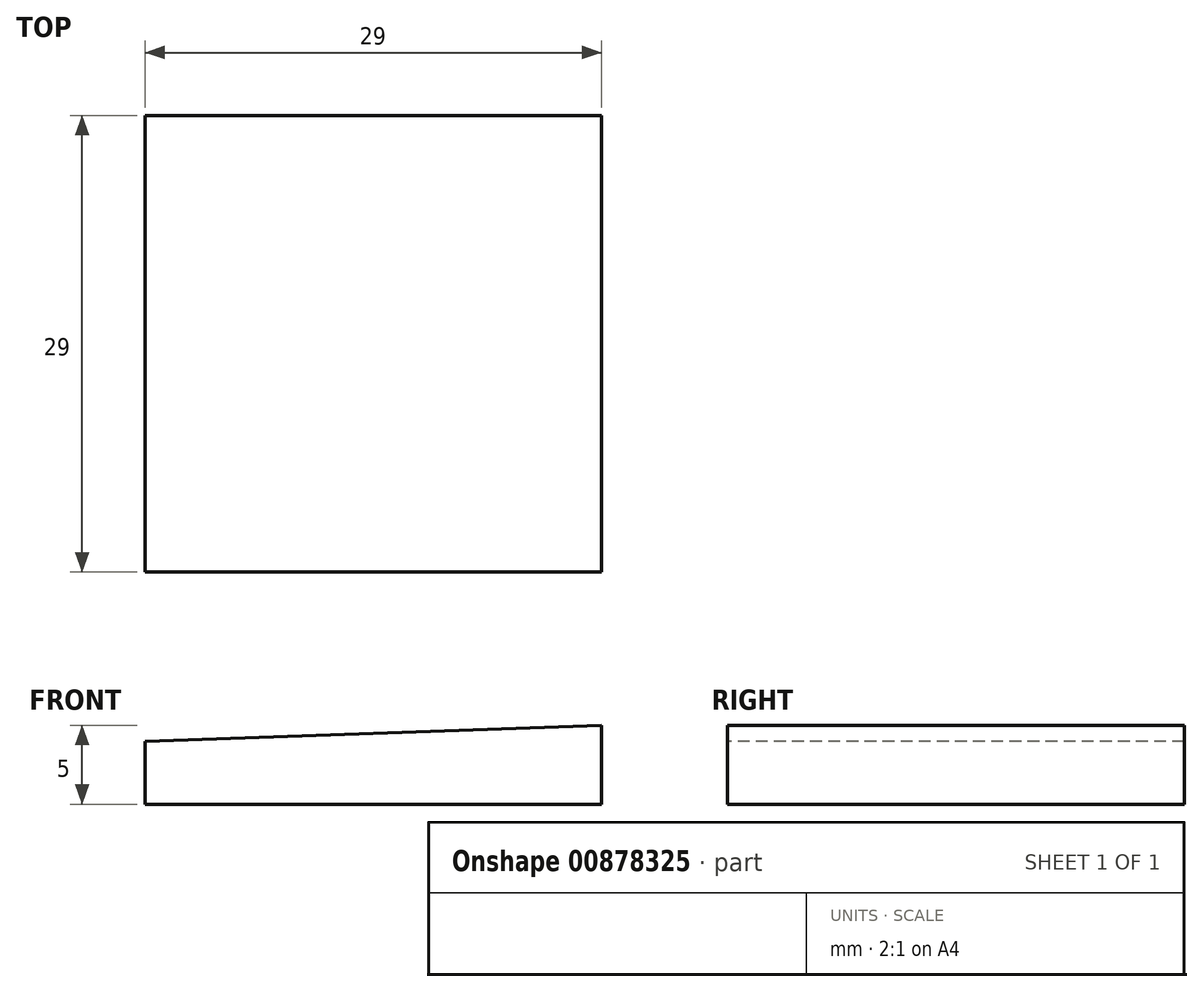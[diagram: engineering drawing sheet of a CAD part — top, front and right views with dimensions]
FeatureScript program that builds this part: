
annotation { "Feature Type Name" : "Feature", "Feature Type Description" : "" }
export const myFeature = defineFeature(function(context is Context, id is Id, definition is map)
    precondition{}
    {
        {
            var Q0;
            Q0=qCreatedBy(makeId("Top.planeOp"),FACE);
            var sketch = newSketch(context, id + "F0", { "sketchPlane" : qUnion([Q0])});
            skLineSegment(sketch, "E0.bottom", {"start": v(14.5, -14.5) * mm, "end": v(-14.5, -14.5) * mm});
            skLineSegment(sketch, "E0.top", {"start": v(14.5, 14.5) * mm, "end": v(-14.5, 14.5) * mm});
            skLineSegment(sketch, "E0.left", {"start": v(14.5, -14.5) * mm, "end": v(14.5, 14.5) * mm});
            skLineSegment(sketch, "E0.right", {"start": v(-14.5, -14.5) * mm, "end": v(-14.5, 14.5) * mm});
            skPoint(sketch, "E0.middle", {"position": v(0, 0) * mm});
            skSolve(sketch);
        }
        {
            var Q0;
            Q0 = qSketchRegion(id + "F0", true);
            extrude(context, id + "F1", {"entities" : qUnion([Q0]), "depth" : 6 * mm, "offsetDistance" : 25 * mm});
        }
        {
            var Q0;
            Q0=makeQuery(id+"F1.opExtrude","SWEPT_FACE",FACE,{"disambiguationData":[OSD([sQuery(id+"F0.wireOp",EDGE,"E0.bottom")])]});
            var sketch = newSketch(context, id + "F2", { "sketchPlane" : qUnion([Q0])});
            skLineSegment(sketch, "E1", {"start": v(-14.5, 4) * mm, "end": v(14.5, 5) * mm});
            skSolve(sketch);
        }
        {
            var Q0;
            {var subQ0=sQuery(id+"F2.wireOp",EDGE,"E1");Q0=makeQuery(id+"F2.imprint","IMPRINT",FACE,{"disambiguationData":[TD([[makeQuery(id+"F2.imprint","IMPRINT",EDGE,{"derivedFrom":subQ0}),1.0]])]});}
            extrude(context, id + "F3", {"entities" : qUnion([Q0]), "operationType" : NewBodyOperationType.REMOVE, "oppositeDirection" : true, "depth" : 29 * mm, "offsetDistance" : 25 * mm});
        }
    });
